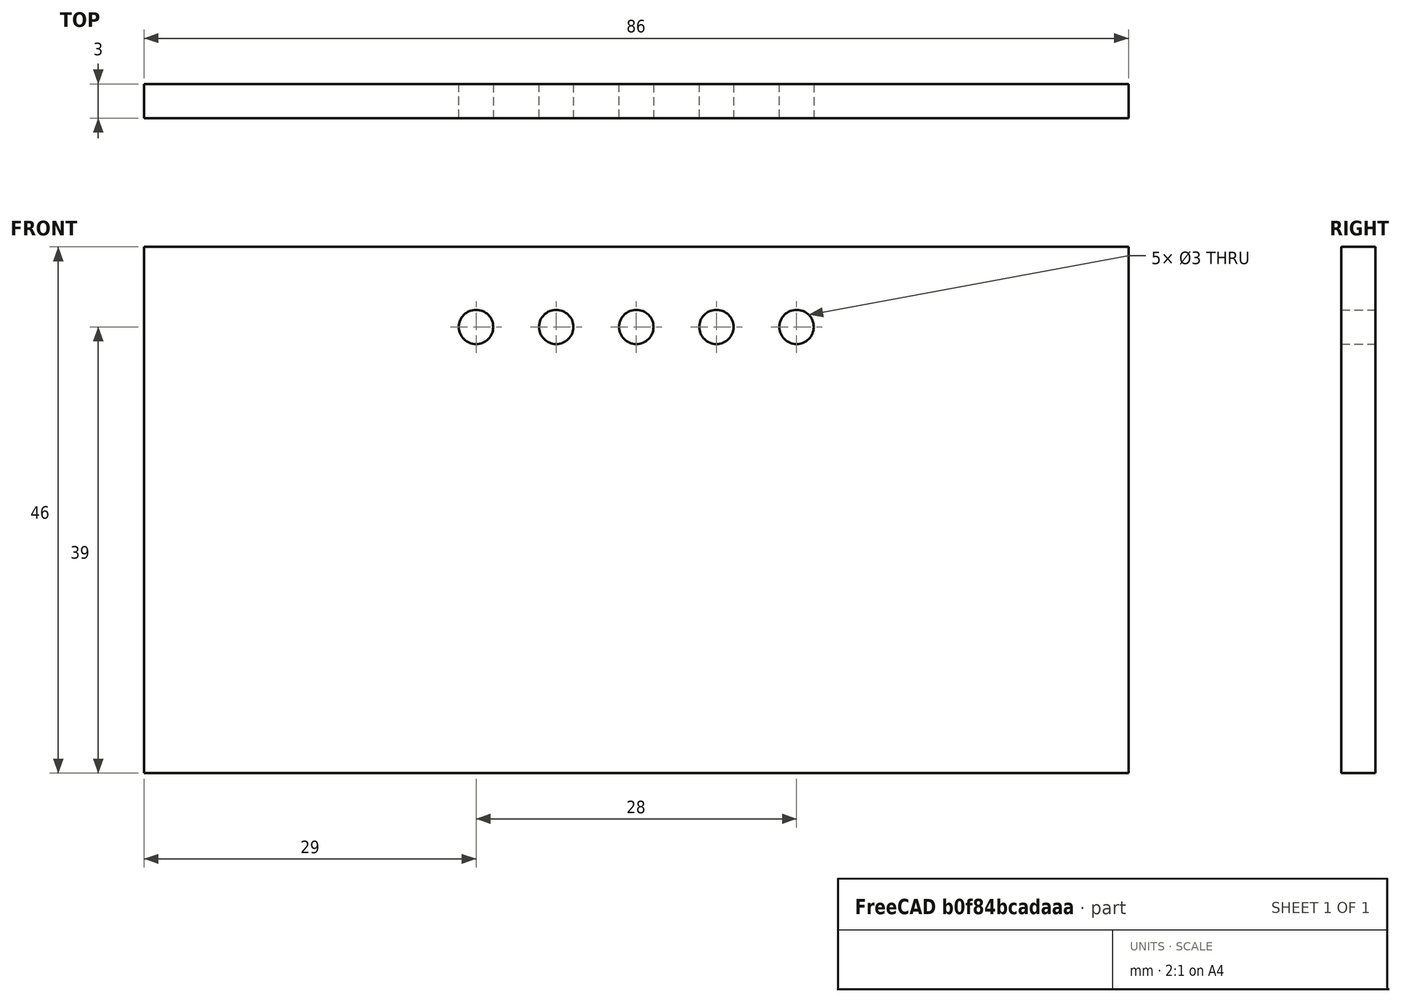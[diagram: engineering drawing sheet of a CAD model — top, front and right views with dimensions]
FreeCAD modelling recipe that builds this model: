
FCSTD DOCUMENT  (FreeCAD 0.20R29410 (Git))
Label: case-side-panel
License: All rights reserved
LicenseURL: http://en.wikipedia.org/wiki/All_rights_reserved
objects: Sketcher::SketchObject×1, PartDesign::Pad×1, PartDesign::Body×1
note: 4 computed .brp shape members not serialized (recipe doc carries the construction recipe); baked Part::Feature solids carry a one-line shape summary decoded from their .brp

FEATURE [Sketcher::SketchObject] Sketch  label="skBase"
  FullyConstrained = true
  MapMode = 5
  Placement = pos=(0,0,0) rot=(1,0,0;1.5708rad)
  Support = -> [XZ_Plane]
  sketch-geometry (12):
    g0: LineSegment StartX=-43 StartY=23 StartZ=0 EndX=43 EndY=23 EndZ=0
    g1: LineSegment StartX=43 StartY=23 StartZ=0 EndX=43 EndY=-23 EndZ=0
    g2: LineSegment StartX=43 StartY=-23 StartZ=0 EndX=-43 EndY=-23 EndZ=0
    g3: LineSegment StartX=-43 StartY=-23 StartZ=0 EndX=-43 EndY=23 EndZ=0
    g4: Circle CenterX=-7 CenterY=16 CenterZ=0 NormalX=0 NormalY=0 NormalZ=1 AngleXU=0 Radius=1.5
    g5: Circle CenterX=0 CenterY=16 CenterZ=0 NormalX=0 NormalY=0 NormalZ=1 AngleXU=0 Radius=1.5
    g6: Circle CenterX=7 CenterY=16 CenterZ=0 NormalX=0 NormalY=0 NormalZ=1 AngleXU=0 Radius=1.5
    g7: LineSegment StartX=0 StartY=16 StartZ=0 EndX=-7 EndY=16 EndZ=0
    g8: LineSegment StartX=-7 StartY=23 StartZ=0 EndX=-7 EndY=16 EndZ=0
    g9: Circle CenterX=14 CenterY=16 CenterZ=0 NormalX=0 NormalY=0 NormalZ=1 AngleXU=0 Radius=1.5
    g10: Circle CenterX=-14 CenterY=16 CenterZ=0 NormalX=0 NormalY=0 NormalZ=1 AngleXU=0 Radius=1.5
    g11: LineSegment StartX=-7 StartY=16 StartZ=0 EndX=-14 EndY=16 EndZ=0
  constraints (30):
    c: Coincident(g0,g1)
    c: Coincident(g1,g2)
    c: Coincident(g2,g3)
    c: Coincident(g3,g0)
    c: Horizontal(g2)
    c: Vertical(g3)
    c: Symmetric(g0,g1,g-1)
    c: Symmetric(g0,g0,g-2)
    c: Distance(g1) = 46
    c: Distance(g0) = 86
    c: Diameter(g5) = 3
    c: Coincident(g7,g5)
    c: Coincident(g7,g4)
    c: Coincident(g8,g4)
    c: Distance(g7) = 7
    c: Symmetric(g6,g4,g5)
    c: PointOnObject(g5,g-2)
    c: PointOnObject(g8,g0)
    c: Vertical(g8)
    c: Horizontal(g7)
    c: Symmetric(g10,g9,g5)
    c: Coincident(g11,g4)
    c: Coincident(g11,g10)
    c: Horizontal(g11)
    c: Equal(g7,g8)
    c: Equal(g8,g11)
    c: Equal(g10,g4)
    c: Equal(g4,g5)
    c: Equal(g5,g6)
    c: Equal(g6,g9)
FEATURE [PartDesign::Pad] Pad  label="pdBase"
  Direction = (0,-1,-2e-16)
  Length = 3
  Length2 = 10
  Placement = pos=(0,0,0) rot=(1,0,0;1.5708rad)
  Profile = -> Sketch
  ReferenceAxis = -> Sketch [N_Axis]
  Type = 0
FEATURE [PartDesign::Body] Body
  Group = -> [Sketch,Pad]
  Origin = -> Origin
  Tip = -> Pad
